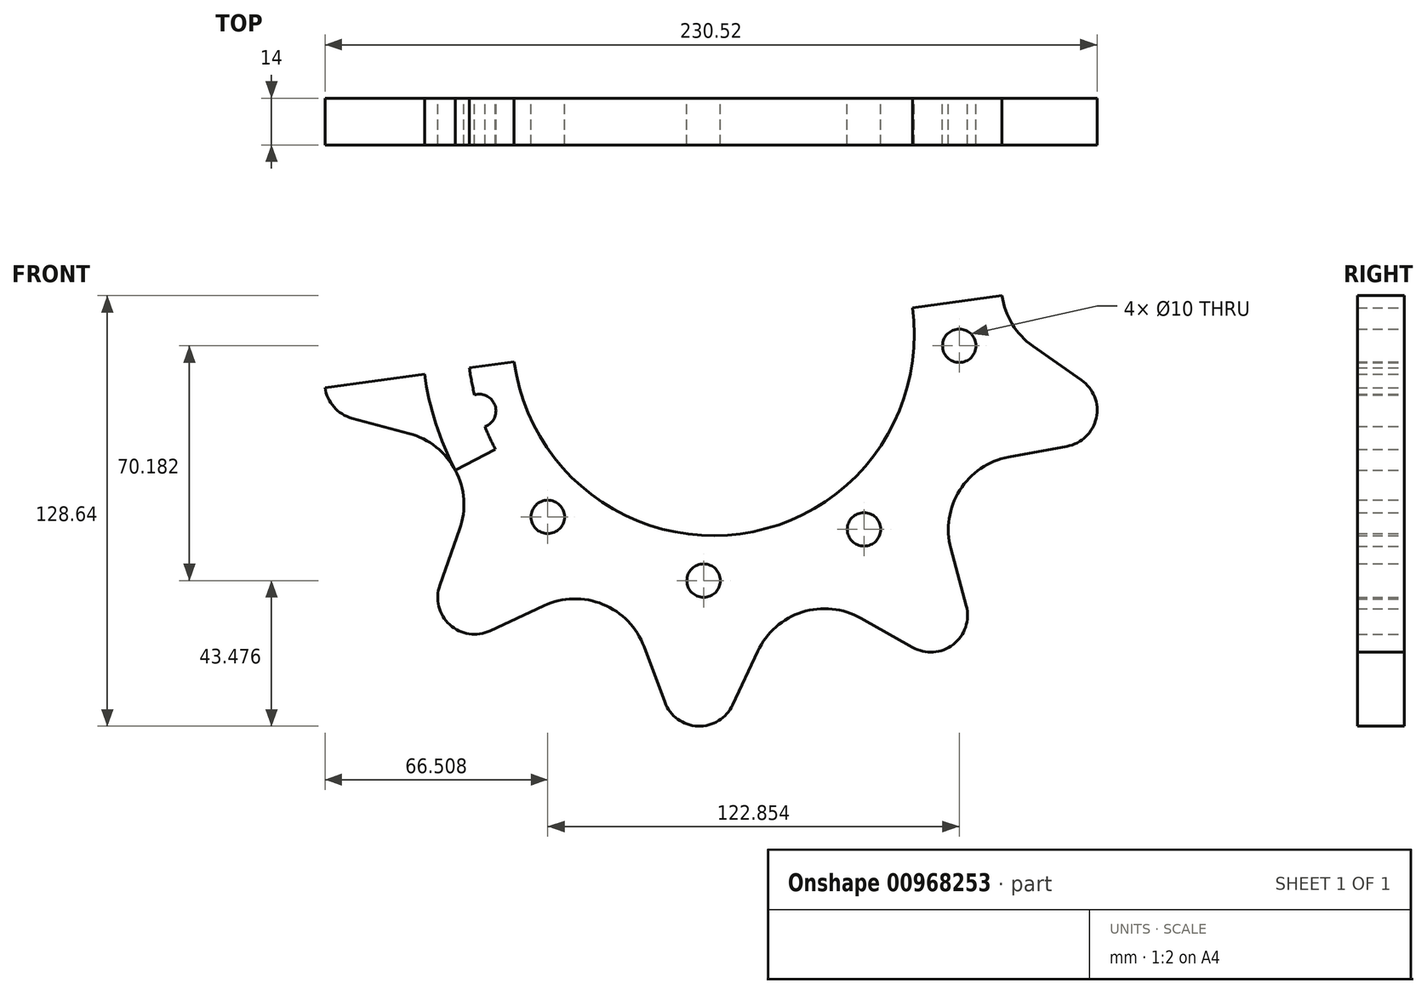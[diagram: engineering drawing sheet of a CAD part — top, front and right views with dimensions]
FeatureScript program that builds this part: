
annotation { "Feature Type Name" : "Feature", "Feature Type Description" : "" }
export const myFeature = defineFeature(function(context is Context, id is Id, definition is map)
    precondition{}
    {
        {
            var Q0;
            Q0=qCreatedBy(makeId("Front.planeOp"),FACE);
            var sketch = newSketch(context, id + "F0", { "sketchPlane" : qUnion([Q0])});
            skCircle(sketch, "E0", {"center": v(-98.07, 54.22) * mm, "radius": 87 * mm});
            skCircle(sketch, "E1", {"center": v(-130.37, 155.18) * mm, "radius": 11 * mm});
            skCircle(sketch, "E2", {"center": v(-57.92, 152.32) * mm, "radius": 11 * mm});
            skCircle(sketch, "E3", {"center": v(-4.25, 103.56) * mm, "radius": 11 * mm});
            skCircle(sketch, "E4", {"center": v(5.52, 31.71) * mm, "radius": 11 * mm});
            skCircle(sketch, "E5", {"center": v(-33.18, -29.6) * mm, "radius": 11 * mm});
            skCircle(sketch, "E6", {"center": v(-102.24, -51.7) * mm, "radius": 11 * mm});
            skCircle(sketch, "E7", {"center": v(-187.7, 110.8) * mm, "radius": 11 * mm});
            skCircle(sketch, "E8", {"center": v(-203.1, 39.94) * mm, "radius": 11 * mm});
            skCircle(sketch, "E9", {"center": v(-169.35, -24.23) * mm, "radius": 11 * mm});
            skLineSegment(sketch, "E10", {"start": v(-98.07, 54.22) * mm, "end": v(-169.35, -24.23) * mm});
            skLineSegment(sketch, "E11", {"start": v(-98.07, 54.22) * mm, "end": v(-102.24, -51.7) * mm});
            skLineSegment(sketch, "E12", {"start": v(-98.07, 54.22) * mm, "end": v(-33.18, -29.6) * mm});
            skLineSegment(sketch, "E13", {"start": v(-98.07, 54.22) * mm, "end": v(5.52, 31.71) * mm});
            skLineSegment(sketch, "E14", {"start": v(-98.07, 54.22) * mm, "end": v(-4.25, 103.56) * mm});
            skLineSegment(sketch, "E15", {"start": v(-98.07, 54.22) * mm, "end": v(-57.92, 152.32) * mm});
            skLineSegment(sketch, "E16", {"start": v(-98.07, 54.22) * mm, "end": v(-130.37, 155.18) * mm});
            skLineSegment(sketch, "E17", {"start": v(-98.07, 54.22) * mm, "end": v(-187.7, 110.8) * mm});
            skLineSegment(sketch, "E18", {"start": v(-98.07, 54.22) * mm, "end": v(-203.1, 39.94) * mm});
            skCircle(sketch, "E19", {"center": v(-93.77, 163.13) * mm, "radius": 22 * mm});
            skCircle(sketch, "E20", {"center": v(-24.77, 134.9) * mm, "radius": 22 * mm});
            skCircle(sketch, "E21", {"center": v(9.94, 68.9) * mm, "radius": 22 * mm});
            skCircle(sketch, "E22", {"center": v(-5.89, -3.96) * mm, "radius": 22 * mm});
            skCircle(sketch, "E23", {"center": v(-164.79, 140.41) * mm, "radius": 22 * mm});
            skCircle(sketch, "E24", {"center": v(-204.58, 77.36) * mm, "radius": 22 * mm});
            skCircle(sketch, "E25", {"center": v(-194.54, 3.48) * mm, "radius": 22 * mm});
            skCircle(sketch, "E26", {"center": v(-139.35, -46.66) * mm, "radius": 22 * mm});
            skCircle(sketch, "E27", {"center": v(-64.85, -49.6) * mm, "radius": 22 * mm});
            skLineSegment(sketch, "E28", {"start": v(-93.77, 163.13) * mm, "end": v(-98.07, 54.22) * mm});
            skLineSegment(sketch, "E29", {"start": v(-98.07, 54.22) * mm, "end": v(-24.77, 134.9) * mm});
            skLineSegment(sketch, "E30", {"start": v(-98.07, 54.22) * mm, "end": v(9.94, 68.9) * mm});
            skLineSegment(sketch, "E31", {"start": v(-98.07, 54.22) * mm, "end": v(-5.89, -3.96) * mm});
            skLineSegment(sketch, "E32", {"start": v(-98.07, 54.22) * mm, "end": v(-64.85, -49.6) * mm});
            skLineSegment(sketch, "E33", {"start": v(-98.07, 54.22) * mm, "end": v(-139.35, -46.66) * mm});
            skLineSegment(sketch, "E34", {"start": v(-98.07, 54.22) * mm, "end": v(-194.54, 3.48) * mm});
            skLineSegment(sketch, "E35", {"start": v(-98.07, 54.22) * mm, "end": v(-204.58, 77.36) * mm});
            skLineSegment(sketch, "E36", {"start": v(-98.07, 54.22) * mm, "end": v(-164.79, 140.41) * mm});
            skLineSegment(sketch, "E37", {"start": v(-141.33, 156.14) * mm, "end": v(-142.87, 138.5) * mm});
            skLineSegment(sketch, "E38", {"start": v(-122, 162.32) * mm, "end": v(-110.5, 148.85) * mm});
            skLineSegment(sketch, "E39", {"start": v(-185.89, 121.64) * mm, "end": v(-168.42, 118.72) * mm});
            skLineSegment(sketch, "E40", {"start": v(-196.72, 104.49) * mm, "end": v(-186.56, 89.98) * mm});
            skLineSegment(sketch, "E41", {"start": v(-208.68, 49.42) * mm, "end": v(-193.42, 58.4) * mm});
            skLineSegment(sketch, "E42", {"start": v(-205.95, 29.31) * mm, "end": v(-188.84, 24.73) * mm});
            skLineSegment(sketch, "E43", {"start": v(-179.72, -20.56) * mm, "end": v(-173.8, -3.87) * mm});
            skLineSegment(sketch, "E44", {"start": v(-164.7, -34.2) * mm, "end": v(-148.65, -26.72) * mm});
            skLineSegment(sketch, "E45", {"start": v(-112.55, -55.55) * mm, "end": v(-118.74, -38.96) * mm});
            skLineSegment(sketch, "E46", {"start": v(-92.27, -56.35) * mm, "end": v(-84.79, -40.3) * mm});
            skLineSegment(sketch, "E47", {"start": v(-38.6, -39.18) * mm, "end": v(-54.01, -30.45) * mm});
            skLineSegment(sketch, "E48", {"start": v(-22.56, -26.76) * mm, "end": v(-27.14, -9.65) * mm});
            skLineSegment(sketch, "E49", {"start": v(7.52, 20.9) * mm, "end": v(-9.9, 17.68) * mm});
            skLineSegment(sketch, "E50", {"start": v(11.83, 40.72) * mm, "end": v(-2.68, 50.88) * mm});
            skLineSegment(sketch, "E51", {"start": v(4.24, 96.56) * mm, "end": v(-7.03, 82.9) * mm});
            skLineSegment(sketch, "E52", {"start": v(-5.2, 114.52) * mm, "end": v(-22.85, 112.98) * mm});
            skLineSegment(sketch, "E53", {"start": v(-46.92, 152.41) * mm, "end": v(-46.77, 134.7) * mm});
            skLineSegment(sketch, "E54", {"start": v(-65.7, 160.1) * mm, "end": v(-78.22, 147.58) * mm});
            skCircle(sketch, "E55", {"center": v(-98.07, 54.22) * mm, "radius": 60 * mm});
            skLineSegment(sketch, "E56", {"start": v(9.94, 68.9) * mm, "end": v(-214, 38.46) * mm});
            skCircle(sketch, "E57", {"center": v(-98.07, 54.22) * mm, "radius": 73.5 * mm});
            skCircle(sketch, "E58", {"center": v(-24.64, 50.96) * mm, "radius": 5 * mm});
            skCircle(sketch, "E59", {"center": v(-53.08, -3.9) * mm, "radius": 5 * mm});
            skCircle(sketch, "E60", {"center": v(-167.97, 31.5) * mm, "radius": 5 * mm});
            skCircle(sketch, "E61", {"center": v(-147.5, -0.18) * mm, "radius": 5 * mm});
            skCircle(sketch, "E62", {"center": v(-100.96, -19.22) * mm, "radius": 5 * mm});
            skSolve(sketch);
        }
        {
            var Q0;
            {var subQ2=sQuery(id+"F0.wireOp",EDGE,"E56");var subQ5=makeQuery(id+"F0.imprint","IMPRINT",VERTEX,{"derivedFrom":subQ2});Q0=makeQuery(id+"F0.imprint","IMPRINT",FACE,{"disambiguationData":[TD([[makeQuery(id+"F0.imprint","IMPRINT",EDGE,{"disambiguationData":[TD([[subQ5,1.0]])],"derivedFrom":subQ2}),1.0]])]});}
            var Q1;
            {var subQ0=sQuery(id+"F0.wireOp",EDGE,"E42");Q1=makeQuery(id+"F0.imprint","IMPRINT",FACE,{"disambiguationData":[TD([[makeQuery(id+"F0.imprint","IMPRINT",EDGE,{"derivedFrom":subQ0}),1.0]])]});}
            var Q2;
            {var subQ3=sQuery(id+"F0.wireOp",EDGE,"E34");var subQ5=sQuery(id+"F0.wireOp",EDGE,"E55");var subQ6=makeQuery(id+"F0.imprint","INTERSECT",VERTEX,{"derivedFrom":[subQ3,subQ5]});Q2=makeQuery(id+"F0.imprint","IMPRINT",FACE,{"disambiguationData":[TD([[makeQuery(id+"F0.imprint","IMPRINT",EDGE,{"disambiguationData":[TD([[subQ6,1.0]])],"derivedFrom":subQ5}),-1.0]])]});}
            var Q3;
            {var subQ0=sQuery(id+"F0.wireOp",EDGE,"E13");var subQ1=sQuery(id+"F0.wireOp",EDGE,"E0");var subQ2=makeQuery(id+"F0.imprint","INTERSECT",VERTEX,{"derivedFrom":[subQ1,subQ0]});Q3=makeQuery(id+"F0.imprint","IMPRINT",FACE,{"disambiguationData":[TD([[makeQuery(id+"F0.imprint","IMPRINT",EDGE,{"disambiguationData":[TD([[subQ2,1.0]])],"derivedFrom":subQ0}),1.0]])]});}
            var Q4;
            {var subQ0=sQuery(id+"F0.wireOp",EDGE,"E50");Q4=makeQuery(id+"F0.imprint","IMPRINT",FACE,{"disambiguationData":[TD([[makeQuery(id+"F0.imprint","IMPRINT",EDGE,{"derivedFrom":subQ0}),1.0]])]});}
            var Q5;
            {var subQ0=sQuery(id+"F0.wireOp",EDGE,"E4");var subQ1=makeQuery(id+"F0.imprint","INTERSECT",VERTEX,{"derivedFrom":[subQ0,sQuery(id+"F0.wireOp",EDGE,"E50")]});Q5=makeQuery(id+"F0.imprint","IMPRINT",FACE,{"disambiguationData":[TD([[makeQuery(id+"F0.imprint","IMPRINT",EDGE,{"disambiguationData":[TD([[subQ1,-1.0]])],"derivedFrom":subQ0}),1.0]])]});}
            var Q6;
            {var subQ0=sQuery(id+"F0.wireOp",EDGE,"E49");Q6=makeQuery(id+"F0.imprint","IMPRINT",FACE,{"disambiguationData":[TD([[makeQuery(id+"F0.imprint","IMPRINT",EDGE,{"derivedFrom":subQ0}),-1.0]])]});}
            var Q7;
            {var subQ0=sQuery(id+"F0.wireOp",EDGE,"E13");var subQ1=sQuery(id+"F0.wireOp",EDGE,"E0");var subQ2=makeQuery(id+"F0.imprint","INTERSECT",VERTEX,{"derivedFrom":[subQ1,subQ0]});Q7=makeQuery(id+"F0.imprint","IMPRINT",FACE,{"disambiguationData":[TD([[makeQuery(id+"F0.imprint","IMPRINT",EDGE,{"disambiguationData":[TD([[subQ2,1.0]])],"derivedFrom":subQ0}),-1.0]])]});}
            var Q8;
            {var subQ0=sQuery(id+"F0.wireOp",EDGE,"E12");var subQ1=sQuery(id+"F0.wireOp",EDGE,"E0");var subQ2=makeQuery(id+"F0.imprint","INTERSECT",VERTEX,{"derivedFrom":[subQ1,subQ0]});Q8=makeQuery(id+"F0.imprint","IMPRINT",FACE,{"disambiguationData":[TD([[makeQuery(id+"F0.imprint","IMPRINT",EDGE,{"disambiguationData":[TD([[subQ2,1.0]])],"derivedFrom":subQ0}),1.0]])]});}
            var Q9;
            {var subQ5=sQuery(id+"F0.wireOp",EDGE,"E48");Q9=makeQuery(id+"F0.imprint","IMPRINT",FACE,{"disambiguationData":[TD([[makeQuery(id+"F0.imprint","IMPRINT",EDGE,{"derivedFrom":subQ5}),1.0]])]});}
            var Q10;
            {var subQ0=sQuery(id+"F0.wireOp",EDGE,"E5");var subQ1=makeQuery(id+"F0.imprint","INTERSECT",VERTEX,{"derivedFrom":[subQ0,sQuery(id+"F0.wireOp",EDGE,"E48")]});Q10=makeQuery(id+"F0.imprint","IMPRINT",FACE,{"disambiguationData":[TD([[makeQuery(id+"F0.imprint","IMPRINT",EDGE,{"disambiguationData":[TD([[subQ1,-1.0]])],"derivedFrom":subQ0}),1.0]])]});}
            var Q11;
            {var subQ0=sQuery(id+"F0.wireOp",EDGE,"E12");var subQ1=sQuery(id+"F0.wireOp",EDGE,"E0");var subQ2=makeQuery(id+"F0.imprint","INTERSECT",VERTEX,{"derivedFrom":[subQ1,subQ0]});Q11=makeQuery(id+"F0.imprint","IMPRINT",FACE,{"disambiguationData":[TD([[makeQuery(id+"F0.imprint","IMPRINT",EDGE,{"disambiguationData":[TD([[subQ2,1.0]])],"derivedFrom":subQ0}),-1.0]])]});}
            var Q12;
            {var subQ0=sQuery(id+"F0.wireOp",EDGE,"E47");Q12=makeQuery(id+"F0.imprint","IMPRINT",FACE,{"disambiguationData":[TD([[makeQuery(id+"F0.imprint","IMPRINT",EDGE,{"derivedFrom":subQ0}),-1.0]])]});}
            var Q13;
            {var subQ0=sQuery(id+"F0.wireOp",EDGE,"E6");var subQ1=makeQuery(id+"F0.imprint","INTERSECT",VERTEX,{"derivedFrom":[subQ0,sQuery(id+"F0.wireOp",EDGE,"E45")]});Q13=makeQuery(id+"F0.imprint","IMPRINT",FACE,{"disambiguationData":[TD([[makeQuery(id+"F0.imprint","IMPRINT",EDGE,{"disambiguationData":[TD([[subQ1,1.0]])],"derivedFrom":subQ0}),1.0]])]});}
            var Q14;
            {var subQ5=sQuery(id+"F0.wireOp",EDGE,"E46");Q14=makeQuery(id+"F0.imprint","IMPRINT",FACE,{"disambiguationData":[TD([[makeQuery(id+"F0.imprint","IMPRINT",EDGE,{"derivedFrom":subQ5}),1.0]])]});}
            var Q15;
            {var subQ0=sQuery(id+"F0.wireOp",EDGE,"E11");var subQ1=sQuery(id+"F0.wireOp",EDGE,"E0");var subQ2=makeQuery(id+"F0.imprint","INTERSECT",VERTEX,{"derivedFrom":[subQ1,subQ0]});Q15=makeQuery(id+"F0.imprint","IMPRINT",FACE,{"disambiguationData":[TD([[makeQuery(id+"F0.imprint","IMPRINT",EDGE,{"disambiguationData":[TD([[subQ2,1.0]])],"derivedFrom":subQ0}),1.0]])]});}
            var Q16;
            {var subQ0=sQuery(id+"F0.wireOp",EDGE,"E11");var subQ1=sQuery(id+"F0.wireOp",EDGE,"E0");var subQ2=makeQuery(id+"F0.imprint","INTERSECT",VERTEX,{"derivedFrom":[subQ1,subQ0]});Q16=makeQuery(id+"F0.imprint","IMPRINT",FACE,{"disambiguationData":[TD([[makeQuery(id+"F0.imprint","IMPRINT",EDGE,{"disambiguationData":[TD([[subQ2,1.0]])],"derivedFrom":subQ0}),-1.0]])]});}
            var Q17;
            {var subQ0=sQuery(id+"F0.wireOp",EDGE,"E45");Q17=makeQuery(id+"F0.imprint","IMPRINT",FACE,{"disambiguationData":[TD([[makeQuery(id+"F0.imprint","IMPRINT",EDGE,{"derivedFrom":subQ0}),-1.0]])]});}
            var Q18;
            {var subQ0=sQuery(id+"F0.wireOp",EDGE,"E44");Q18=makeQuery(id+"F0.imprint","IMPRINT",FACE,{"disambiguationData":[TD([[makeQuery(id+"F0.imprint","IMPRINT",EDGE,{"derivedFrom":subQ0}),1.0]])]});}
            var Q19;
            {var subQ0=sQuery(id+"F0.wireOp",EDGE,"E9");var subQ1=makeQuery(id+"F0.imprint","INTERSECT",VERTEX,{"derivedFrom":[subQ0,sQuery(id+"F0.wireOp",EDGE,"E43")]});Q19=makeQuery(id+"F0.imprint","IMPRINT",FACE,{"disambiguationData":[TD([[makeQuery(id+"F0.imprint","IMPRINT",EDGE,{"disambiguationData":[TD([[subQ1,1.0]])],"derivedFrom":subQ0}),1.0]])]});}
            var Q20;
            {var subQ5=sQuery(id+"F0.wireOp",EDGE,"E43");Q20=makeQuery(id+"F0.imprint","IMPRINT",FACE,{"disambiguationData":[TD([[makeQuery(id+"F0.imprint","IMPRINT",EDGE,{"derivedFrom":subQ5}),-1.0]])]});}
            var Q21;
            {var subQ0=sQuery(id+"F0.wireOp",EDGE,"E10");var subQ1=sQuery(id+"F0.wireOp",EDGE,"E0");var subQ2=makeQuery(id+"F0.imprint","INTERSECT",VERTEX,{"derivedFrom":[subQ1,subQ0]});Q21=makeQuery(id+"F0.imprint","IMPRINT",FACE,{"disambiguationData":[TD([[makeQuery(id+"F0.imprint","IMPRINT",EDGE,{"disambiguationData":[TD([[subQ2,1.0]])],"derivedFrom":subQ0}),1.0]])]});}
            var Q22;
            {var subQ0=sQuery(id+"F0.wireOp",EDGE,"E10");var subQ1=sQuery(id+"F0.wireOp",EDGE,"E0");var subQ2=makeQuery(id+"F0.imprint","INTERSECT",VERTEX,{"derivedFrom":[subQ1,subQ0]});Q22=makeQuery(id+"F0.imprint","IMPRINT",FACE,{"disambiguationData":[TD([[makeQuery(id+"F0.imprint","IMPRINT",EDGE,{"disambiguationData":[TD([[subQ2,1.0]])],"derivedFrom":subQ0}),-1.0]])]});}
            var Q23;
            {var subQ1=sQuery(id+"F0.wireOp",EDGE,"E56");var subQ5=sQuery(id+"F0.wireOp",EDGE,"E0");var subQ6=makeQuery(id+"F0.imprint","INTERSECT",VERTEX,{"derivedFrom":[subQ5,subQ1]});Q23=makeQuery(id+"F0.imprint","IMPRINT",FACE,{"disambiguationData":[TD([[makeQuery(id+"F0.imprint","IMPRINT",EDGE,{"disambiguationData":[TD([[subQ6,1.0]])],"derivedFrom":subQ1}),1.0]])]});}
            var Q24;
            {var subQ5=sQuery(id+"F0.wireOp",EDGE,"E55");var subQ7=sQuery(id+"F0.wireOp",EDGE,"E10");var subQ8=makeQuery(id+"F0.imprint","INTERSECT",VERTEX,{"derivedFrom":[subQ7,subQ5]});Q24=makeQuery(id+"F0.imprint","IMPRINT",FACE,{"disambiguationData":[TD([[makeQuery(id+"F0.imprint","IMPRINT",EDGE,{"disambiguationData":[TD([[subQ8,-1.0]])],"derivedFrom":subQ7}),-1.0]])]});}
            var Q25;
            {var subQ5=sQuery(id+"F0.wireOp",EDGE,"E55");var subQ6=sQuery(id+"F0.wireOp",EDGE,"E10");var subQ7=makeQuery(id+"F0.imprint","INTERSECT",VERTEX,{"derivedFrom":[subQ6,subQ5]});Q25=makeQuery(id+"F0.imprint","IMPRINT",FACE,{"disambiguationData":[TD([[makeQuery(id+"F0.imprint","IMPRINT",EDGE,{"disambiguationData":[TD([[subQ7,-1.0]])],"derivedFrom":subQ6}),1.0]])]});}
            var Q26;
            {var subQ5=sQuery(id+"F0.wireOp",EDGE,"E55");var subQ6=sQuery(id+"F0.wireOp",EDGE,"E11");var subQ7=makeQuery(id+"F0.imprint","INTERSECT",VERTEX,{"derivedFrom":[subQ6,subQ5]});Q26=makeQuery(id+"F0.imprint","IMPRINT",FACE,{"disambiguationData":[TD([[makeQuery(id+"F0.imprint","IMPRINT",EDGE,{"disambiguationData":[TD([[subQ7,-1.0]])],"derivedFrom":subQ6}),-1.0]])]});}
            var Q27;
            {var subQ5=sQuery(id+"F0.wireOp",EDGE,"E55");var subQ6=sQuery(id+"F0.wireOp",EDGE,"E11");var subQ7=makeQuery(id+"F0.imprint","INTERSECT",VERTEX,{"derivedFrom":[subQ6,subQ5]});Q27=makeQuery(id+"F0.imprint","IMPRINT",FACE,{"disambiguationData":[TD([[makeQuery(id+"F0.imprint","IMPRINT",EDGE,{"disambiguationData":[TD([[subQ7,-1.0]])],"derivedFrom":subQ6}),1.0]])]});}
            var Q28;
            {var subQ0=sQuery(id+"F0.wireOp",EDGE,"E55");var subQ1=sQuery(id+"F0.wireOp",EDGE,"E12");var subQ2=makeQuery(id+"F0.imprint","INTERSECT",VERTEX,{"derivedFrom":[subQ1,subQ0]});Q28=makeQuery(id+"F0.imprint","IMPRINT",FACE,{"disambiguationData":[TD([[makeQuery(id+"F0.imprint","IMPRINT",EDGE,{"disambiguationData":[TD([[subQ2,-1.0]])],"derivedFrom":subQ1}),-1.0]])]});}
            var Q29;
            {var subQ0=sQuery(id+"F0.wireOp",EDGE,"E55");var subQ1=sQuery(id+"F0.wireOp",EDGE,"E12");var subQ2=makeQuery(id+"F0.imprint","INTERSECT",VERTEX,{"derivedFrom":[subQ1,subQ0]});Q29=makeQuery(id+"F0.imprint","IMPRINT",FACE,{"disambiguationData":[TD([[makeQuery(id+"F0.imprint","IMPRINT",EDGE,{"disambiguationData":[TD([[subQ2,-1.0]])],"derivedFrom":subQ1}),1.0]])]});}
            var Q30;
            {var subQ0=sQuery(id+"F0.wireOp",EDGE,"E55");var subQ1=sQuery(id+"F0.wireOp",EDGE,"E13");var subQ2=makeQuery(id+"F0.imprint","INTERSECT",VERTEX,{"derivedFrom":[subQ1,subQ0]});Q30=makeQuery(id+"F0.imprint","IMPRINT",FACE,{"disambiguationData":[TD([[makeQuery(id+"F0.imprint","IMPRINT",EDGE,{"disambiguationData":[TD([[subQ2,-1.0]])],"derivedFrom":subQ1}),-1.0]])]});}
            var Q31;
            {var subQ1=sQuery(id+"F0.wireOp",EDGE,"E55");var subQ7=sQuery(id+"F0.wireOp",EDGE,"E13");var subQ8=makeQuery(id+"F0.imprint","INTERSECT",VERTEX,{"derivedFrom":[subQ7,subQ1]});Q31=makeQuery(id+"F0.imprint","IMPRINT",FACE,{"disambiguationData":[TD([[makeQuery(id+"F0.imprint","IMPRINT",EDGE,{"disambiguationData":[TD([[subQ8,-1.0]])],"derivedFrom":subQ7}),1.0]])]});}
            extrude(context, id + "F1", {"entities" : qUnion([Q0, Q1, Q2, Q3, Q4, Q5, Q6, Q7, Q8, Q9, Q10, Q11, Q12, Q13, Q14, Q15, Q16, Q17, Q18, Q19, Q20, Q21, Q22, Q23, Q24, Q25, Q26, Q27, Q28, Q29, Q30, Q31]), "depth" : 14 * mm, "offsetDistance" : 25 * mm});
        }
    });
